annotation { "Feature Type Name" : "Feature", "Feature Type Description" : "" }
export const myFeature = defineFeature(function(context is Context, id is Id, definition is map)
    precondition{}
    {
        {
            var Q0;
            Q0=qCreatedBy(makeId("Top.planeOp"),FACE);
            var sketch = newSketch(context, id + "F0", { "sketchPlane" : qUnion([Q0])});
            skLineSegment(sketch, "E0", {"start": v(0, 46.67) * mm, "end": v(-9.9, 38.73) * mm});
            skLineSegment(sketch, "E1", {"start": v(-9.9, 38.73) * mm, "end": v(-9.9, 7.95) * mm});
            skLineSegment(sketch, "E2", {"start": v(-9.9, 7.95) * mm, "end": v(0, 0) * mm});
            skLineSegment(sketch, "E3.left", {"start": v(-6.6, 38.73) * mm, "end": v(-6.6, 7.95) * mm});
            skLineSegment(sketch, "E3.right", {"start": v(-3.3, 38.73) * mm, "end": v(-3.3, 7.95) * mm});
            skArc(sketch, "E4", {"start": v(-6.6, 38.73) * mm, "mid": v(-4.95, 40.38) * mm, "end": v(-3.3, 38.73) * mm});
            skArc(sketch, "E5", {"start": v(-6.6, 7.95) * mm, "mid": v(-4.95, 6.3) * mm, "end": v(-3.3, 7.95) * mm});
            skLineSegment(sketch, "E6.bottom", {"start": v(0, 46.67) * mm, "end": v(72.9, 46.67) * mm});
            skLineSegment(sketch, "E6.top", {"start": v(0, 0) * mm, "end": v(72.9, 0) * mm});
            skLineSegment(sketch, "E6.right", {"start": v(76.2, 43.37) * mm, "end": v(76.2, 3.3) * mm});
            skArc(sketch, "E7.filletArc", {"start": v(76.2, 43.37) * mm, "mid": v(75.23, 45.7) * mm, "end": v(72.9, 46.67) * mm});
            skArc(sketch, "E8.filletArc", {"start": v(72.9, 0) * mm, "mid": v(75.23, 0.97) * mm, "end": v(76.2, 3.3) * mm});
            skSolve(sketch);
        }
        {
            var Q0;
            Q0 = qSketchRegion(id + "F0", true);
            extrude(context, id + "F1", {"entities" : qUnion([Q0]), "depth" : 5.08 * mm, "offsetDistance" : 25.4 * mm});
        }
        {
            var Q0;
            Q0=makeQuery(id+"F1.opExtrude","CAP_FACE",FACE,{"disambiguationData":[OSD([sQuery(id+"F0.wireOp",EDGE,"E0"),sQuery(id+"F0.wireOp",EDGE,"E1"),sQuery(id+"F0.wireOp",EDGE,"E2"),sQuery(id+"F0.wireOp",EDGE,"E3.left"),sQuery(id+"F0.wireOp",EDGE,"E3.right"),sQuery(id+"F0.wireOp",EDGE,"E4"),sQuery(id+"F0.wireOp",EDGE,"E5"),sQuery(id+"F0.wireOp",EDGE,"E6.bottom"),sQuery(id+"F0.wireOp",EDGE,"E6.top"),sQuery(id+"F0.wireOp",EDGE,"E6.right"),sQuery(id+"F0.wireOp",EDGE,"E7.filletArc"),sQuery(id+"F0.wireOp",EDGE,"E8.filletArc")])],"isStart":false});
            var sketch = newSketch(context, id + "F2", { "sketchPlane" : qUnion([Q0])});
            skLineSegment(sketch, "E9.bottom", {"start": v(3.3, 43.38) * mm, "end": v(69.6, 43.38) * mm});
            skLineSegment(sketch, "E9.top", {"start": v(3.3, 3.3) * mm, "end": v(69.6, 3.3) * mm});
            skLineSegment(sketch, "E9.left", {"start": v(0, 40.08) * mm, "end": v(0, 6.6) * mm});
            skLineSegment(sketch, "E9.right", {"start": v(72.9, 40.08) * mm, "end": v(72.9, 6.6) * mm});
            skPoint(sketch, "E10.visualSharp", {"position": v(0, 43.38) * mm});
            skArc(sketch, "E10.filletArc", {"start": v(3.3, 43.38) * mm, "mid": v(0.97, 42.42) * mm, "end": v(0, 40.08) * mm});
            skPoint(sketch, "E11.visualSharp", {"position": v(72.9, 43.38) * mm});
            skArc(sketch, "E11.filletArc", {"start": v(72.9, 40.08) * mm, "mid": v(71.93, 42.42) * mm, "end": v(69.6, 43.38) * mm});
            skPoint(sketch, "E12.visualSharp", {"position": v(72.9, 3.3) * mm});
            skArc(sketch, "E12.filletArc", {"start": v(69.6, 3.3) * mm, "mid": v(71.93, 4.27) * mm, "end": v(72.9, 6.6) * mm});
            skPoint(sketch, "E13.visualSharp", {"position": v(0, 3.3) * mm});
            skArc(sketch, "E13.filletArc", {"start": v(0, 6.6) * mm, "mid": v(0.97, 4.27) * mm, "end": v(3.3, 3.3) * mm});
            skLineSegment(sketch, "E14.bottom", {"start": v(6.6, 40.08) * mm, "end": v(66.3, 40.08) * mm});
            skLineSegment(sketch, "E14.top", {"start": v(6.6, 6.6) * mm, "end": v(66.3, 6.6) * mm});
            skLineSegment(sketch, "E14.left", {"start": v(3.3, 36.78) * mm, "end": v(3.3, 9.9) * mm});
            skLineSegment(sketch, "E14.right", {"start": v(69.6, 36.78) * mm, "end": v(69.6, 9.9) * mm});
            skArc(sketch, "E15.filletArc", {"start": v(69.6, 36.78) * mm, "mid": v(68.63, 39.11) * mm, "end": v(66.3, 40.08) * mm});
            skArc(sketch, "E16.filletArc", {"start": v(66.3, 6.6) * mm, "mid": v(68.63, 7.57) * mm, "end": v(69.6, 9.9) * mm});
            skArc(sketch, "E17.filletArc", {"start": v(3.3, 9.9) * mm, "mid": v(4.27, 7.57) * mm, "end": v(6.6, 6.6) * mm});
            skArc(sketch, "E18.filletArc", {"start": v(6.6, 40.08) * mm, "mid": v(4.27, 39.11) * mm, "end": v(3.3, 36.78) * mm});
            skSolve(sketch);
        }
        {
            var Q0;
            Q0=makeQuery(id+"F2.imprint","IMPRINT",FACE,{"disambiguationData":[TD([[makeQuery(id+"F2.imprint","IMPRINT",EDGE,{"derivedFrom":sQuery(id+"F2.wireOp",EDGE,"E9.bottom")}),-1.0]])]});
            extrude(context, id + "F3", {"entities" : qUnion([Q0]), "operationType" : NewBodyOperationType.REMOVE, "oppositeDirection" : true, "depth" : 0.5 * mm, "offsetDistance" : 25.4 * mm});
        }
        {
            var Q0;
            Q0=makeQuery(id+"F1.opExtrude","CAP_EDGE",EDGE,{"disambiguationData":[OSD([sQuery(id+"F0.wireOp",EDGE,"E6.top")])],"isStart":false});
            fillet(context, id + "F4", {"entities" : qUnion([Q0]), "radius" : 0.76 * mm, "tangentPropagation" : true, "allowEdgeOverflow" : false});
        }
        {
            var Q0;
            Q0=makeQuery(id+"F1.opExtrude","CAP_EDGE",EDGE,{"disambiguationData":[OSD([sQuery(id+"F0.wireOp",EDGE,"E1")])],"isStart":false});
            fillet(context, id + "F5", {"entities" : qUnion([Q0]), "radius" : 0.76 * mm, "tangentPropagation" : true, "allowEdgeOverflow" : false});
        }
        {
            var Q0;
            Q0=makeQuery(id+"F1.opExtrude","CAP_EDGE",EDGE,{"disambiguationData":[OSD([sQuery(id+"F0.wireOp",EDGE,"E2")])],"isStart":false});
            var Q1;
            Q1=makeQuery(id+"F1.opExtrude","CAP_EDGE",EDGE,{"disambiguationData":[OSD([sQuery(id+"F0.wireOp",EDGE,"E0")])],"isStart":false});
            fillet(context, id + "F6", {"entities" : qUnion([Q0, Q1]), "radius" : 0.76 * mm, "tangentPropagation" : true, "allowEdgeOverflow" : false});
        }
        {
            var Q0;
            Q0=makeQuery(id+"F3.boolean.opBoolean","SPLIT",FACE,{"disambiguationData":[TD([makeQuery(id+"F3.opExtrude","SWEPT_FACE",FACE,{"disambiguationData":[OSD([sQuery(id+"F2.wireOp",EDGE,"E14.bottom")])]})])],"derivedFrom":makeQuery(id+"F1.opExtrude","CAP_FACE",FACE,{"disambiguationData":[OSD([sQuery(id+"F0.wireOp",EDGE,"E0"),sQuery(id+"F0.wireOp",EDGE,"E1"),sQuery(id+"F0.wireOp",EDGE,"E2"),sQuery(id+"F0.wireOp",EDGE,"E3.left"),sQuery(id+"F0.wireOp",EDGE,"E3.right"),sQuery(id+"F0.wireOp",EDGE,"E4"),sQuery(id+"F0.wireOp",EDGE,"E5"),sQuery(id+"F0.wireOp",EDGE,"E6.bottom"),sQuery(id+"F0.wireOp",EDGE,"E6.top"),sQuery(id+"F0.wireOp",EDGE,"E6.right"),sQuery(id+"F0.wireOp",EDGE,"E7.filletArc"),sQuery(id+"F0.wireOp",EDGE,"E8.filletArc")])],"isStart":false})});
            var sketch = newSketch(context, id + "F7", { "sketchPlane" : qUnion([Q0])});
            skText(sketch, "E19", { "text": "Jude Irons", "fontName": "OpenSans-BoldItalic.ttf"});
            const initialGuessF7  = {"E19": [0.00606, 0.00965, 1, 0, 0.00628]};
            skSetInitialGuess(sketch, initialGuessF7);
            skSolve(sketch);
        }
        {
            var Q0;
            Q0 = qSketchRegion(id + "F7", true);
            extrude(context, id + "F8", {"entities" : qUnion([Q0]), "operationType" : NewBodyOperationType.REMOVE, "oppositeDirection" : true, "depth" : 0.5 * mm, "offsetDistance" : 25.4 * mm});
        }
    });